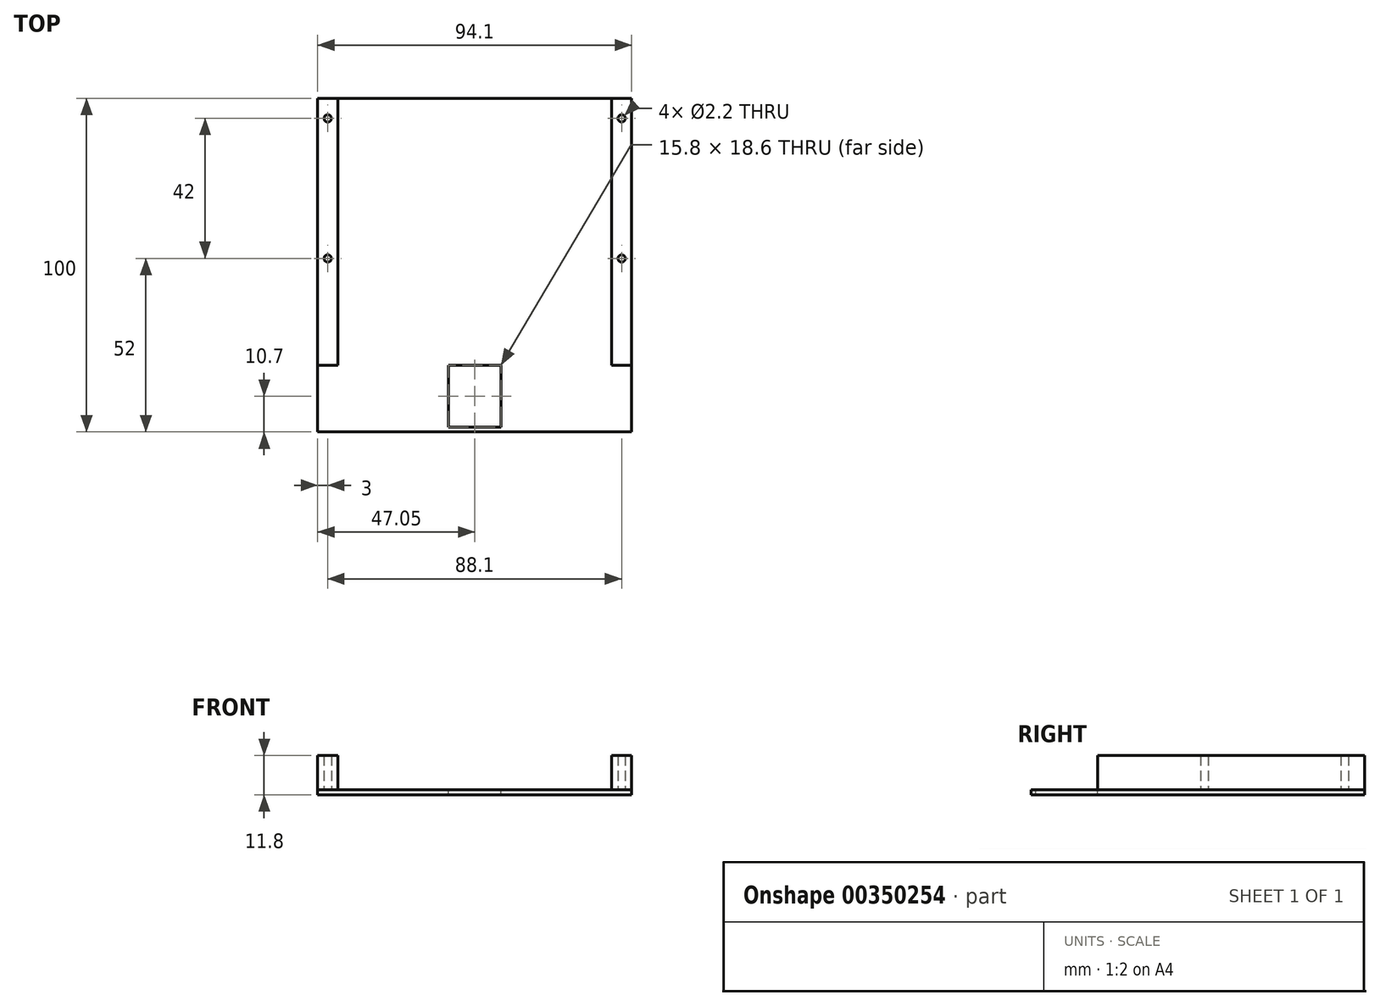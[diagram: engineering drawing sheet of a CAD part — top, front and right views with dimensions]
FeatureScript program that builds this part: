
annotation { "Feature Type Name" : "Feature", "Feature Type Description" : "" }
export const myFeature = defineFeature(function(context is Context, id is Id, definition is map)
    precondition{}
    {
        {
            var Q0;
            Q0=qCreatedBy(makeId("Top.planeOp"),FACE);
            var sketch = newSketch(context, id + "F0", { "sketchPlane" : qUnion([Q0])});
            skLineSegment(sketch, "E0.bottom", {"start": v(0, 0) * mm, "end": v(82.1, 0) * mm});
            skLineSegment(sketch, "E0.top", {"start": v(0, 80) * mm, "end": v(82.1, 80) * mm});
            skLineSegment(sketch, "E0.left", {"start": v(0, 0) * mm, "end": v(0, 80) * mm});
            skLineSegment(sketch, "E0.right", {"start": v(82.1, 0) * mm, "end": v(82.1, 80) * mm});
            skLineSegment(sketch, "E1.bottom", {"start": v(82.1, 80) * mm, "end": v(88.1, 80) * mm});
            skLineSegment(sketch, "E1.top", {"start": v(82.1, 0) * mm, "end": v(88.1, 0) * mm});
            skLineSegment(sketch, "E1.left", {"start": v(82.1, 80) * mm, "end": v(82.1, 0) * mm});
            skLineSegment(sketch, "E1.right", {"start": v(88.1, 80) * mm, "end": v(88.1, 0) * mm});
            skLineSegment(sketch, "E2.bottom", {"start": v(0, 0) * mm, "end": v(-6, 0) * mm});
            skLineSegment(sketch, "E2.top", {"start": v(0, 80) * mm, "end": v(-6, 80) * mm});
            skLineSegment(sketch, "E2.right", {"start": v(-6, 0) * mm, "end": v(-6, 80) * mm});
            skLineSegment(sketch, "E3.bottom", {"start": v(-6, 0) * mm, "end": v(88.1, 0) * mm});
            skLineSegment(sketch, "E3.top", {"start": v(-6, -20) * mm, "end": v(88.1, -20) * mm});
            skLineSegment(sketch, "E3.left", {"start": v(-6, 0) * mm, "end": v(-6, -20) * mm});
            skLineSegment(sketch, "E3.right", {"start": v(88.1, 0) * mm, "end": v(88.1, -20) * mm});
            skLineSegment(sketch, "E4.bottom", {"start": v(-6, 0) * mm, "end": v(33.15, 0) * mm});
            skLineSegment(sketch, "E4.top", {"start": v(-6, -20) * mm, "end": v(33.15, -20) * mm});
            skLineSegment(sketch, "E4.right", {"start": v(33.15, 0) * mm, "end": v(33.15, -20) * mm});
            skLineSegment(sketch, "E5.bottom", {"start": v(88.1, 0) * mm, "end": v(48.95, 0) * mm});
            skLineSegment(sketch, "E5.top", {"start": v(88.1, -20) * mm, "end": v(48.95, -20) * mm});
            skLineSegment(sketch, "E5.right", {"start": v(48.95, 0) * mm, "end": v(48.95, -20) * mm});
            skLineSegment(sketch, "E6.bottom", {"start": v(33.15, 0) * mm, "end": v(48.95, 0) * mm});
            skLineSegment(sketch, "E6.top", {"start": v(33.15, -20) * mm, "end": v(48.95, -20) * mm});
            skLineSegment(sketch, "E7.top", {"start": v(33.15, -18.6) * mm, "end": v(48.95, -18.6) * mm});
            skLineSegment(sketch, "E7.left", {"start": v(33.15, 0) * mm, "end": v(33.15, -18.6) * mm});
            skLineSegment(sketch, "E7.right", {"start": v(48.95, 0) * mm, "end": v(48.95, -18.6) * mm});
            skLineSegment(sketch, "E8.bottom", {"start": v(33.15, -18.6) * mm, "end": v(38.15, -18.6) * mm});
            skLineSegment(sketch, "E8.top", {"start": v(33.15, -20) * mm, "end": v(38.15, -20) * mm});
            skLineSegment(sketch, "E8.left", {"start": v(33.15, -18.6) * mm, "end": v(33.15, -20) * mm});
            skLineSegment(sketch, "E8.right", {"start": v(38.15, -18.6) * mm, "end": v(38.15, -20) * mm});
            skLineSegment(sketch, "E9.bottom", {"start": v(48.95, -18.6) * mm, "end": v(43.95, -18.6) * mm});
            skLineSegment(sketch, "E9.top", {"start": v(48.95, -20) * mm, "end": v(43.95, -20) * mm});
            skLineSegment(sketch, "E9.left", {"start": v(48.95, -18.6) * mm, "end": v(48.95, -20) * mm});
            skLineSegment(sketch, "E9.right", {"start": v(43.95, -18.6) * mm, "end": v(43.95, -20) * mm});
            skLineSegment(sketch, "E10.bottom", {"start": v(38.15, -18.6) * mm, "end": v(43.95, -18.6) * mm});
            skLineSegment(sketch, "E10.top", {"start": v(38.15, -20) * mm, "end": v(43.95, -20) * mm});
            skPoint(sketch, "E11", {"position": v(-3, 74) * mm});
            skPoint(sketch, "E11.positionSnap0", {"position": v(-3, 80) * mm});
            skPoint(sketch, "E12", {"position": v(85.1, 74) * mm});
            skPoint(sketch, "E12.positionSnap0", {"position": v(85.1, 80) * mm});
            skPoint(sketch, "E13", {"position": v(-3, -10) * mm});
            skPoint(sketch, "E13.positionSnap0", {"position": v(-6, -10) * mm});
            skPoint(sketch, "E14.positionSnap0", {"position": v(88.1, -10) * mm});
            skPoint(sketch, "E15", {"position": v(54.95, -10) * mm});
            skPoint(sketch, "E15.positionSnap0", {"position": v(48.95, -10) * mm});
            skPoint(sketch, "E16", {"position": v(27.15, -10) * mm});
            skPoint(sketch, "E16.positionSnap0", {"position": v(33.15, -10) * mm});
            skPoint(sketch, "E17", {"position": v(85.1, -10) * mm});
            skLineSegment(sketch, "E18", {"start": v(85.1, 74) * mm, "end": v(85.1, -10) * mm, "construction": true});
            skLineSegment(sketch, "E19", {"start": v(-3, 74) * mm, "end": v(-3, -10) * mm, "construction": true});
            skPoint(sketch, "E20", {"position": v(85.1, 32) * mm});
            skPoint(sketch, "E21", {"position": v(-3, 32) * mm});
            skSolve(sketch);
        }
        {
            var Q0;
            Q0=makeQuery(id+"F0.imprint","IMPRINT",FACE,{"disambiguationData":[TD([[makeQuery(id+"F0.imprint","IMPRINT",EDGE,{"derivedFrom":sQuery(id+"F0.wireOp",EDGE,"E2.top")}),1.0]])]});
            var Q1;
            Q1=makeQuery(id+"F0.imprint","IMPRINT",FACE,{"disambiguationData":[TD([[makeQuery(id+"F0.imprint","IMPRINT",EDGE,{"derivedFrom":sQuery(id+"F0.wireOp",EDGE,"E4.top")}),1.0]])]});
            var Q2;
            Q2=makeQuery(id+"F0.imprint","IMPRINT",FACE,{"disambiguationData":[TD([[makeQuery(id+"F0.imprint","IMPRINT",EDGE,{"derivedFrom":sQuery(id+"F0.wireOp",EDGE,"E6.top")}),1.0]])]});
            var Q3;
            Q3=makeQuery(id+"F0.imprint","IMPRINT",FACE,{"disambiguationData":[TD([[makeQuery(id+"F0.imprint","IMPRINT",EDGE,{"derivedFrom":sQuery(id+"F0.wireOp",EDGE,"E5.top")}),-1.0]])]});
            var Q4;
            Q4=makeQuery(id+"F0.imprint","IMPRINT",FACE,{"disambiguationData":[TD([[makeQuery(id+"F0.imprint","IMPRINT",EDGE,{"derivedFrom":sQuery(id+"F0.wireOp",EDGE,"E1.bottom")}),-1.0]])]});
            var Q5;
            Q5=makeQuery(id+"F0.imprint","IMPRINT",FACE,{"disambiguationData":[TD([[makeQuery(id+"F0.imprint","IMPRINT",EDGE,{"derivedFrom":sQuery(id+"F0.wireOp",EDGE,"E8.bottom")}),-1.0]])]});
            var Q6;
            Q6=makeQuery(id+"F0.imprint","IMPRINT",FACE,{"disambiguationData":[TD([[makeQuery(id+"F0.imprint","IMPRINT",EDGE,{"derivedFrom":sQuery(id+"F0.wireOp",EDGE,"E9.bottom")}),1.0]])]});
            extrude(context, id + "F1", {"entities" : qUnion([Q0, Q1, Q2, Q3, Q4, Q5, Q6]), "offsetDistance" : 25 * mm, "depth" : 10.3 * mm});
        }
        {
            var Q0;
            Q0 = qSketchRegion(id + "F0", true);
            var Q1;
            Q1=makeQuery(id+"F0.imprint","IMPRINT",FACE,{"disambiguationData":[TD([[makeQuery(id+"F0.imprint","IMPRINT",EDGE,{"derivedFrom":sQuery(id+"F0.wireOp",EDGE,"E6.bottom")}),-1.0]])]});
            extrude(context, id + "F2", {"entities" : qUnion([Q0, Q1]), "oppositeDirection" : true, "offsetDistance" : 25 * mm, "depth" : 1.5 * mm});
        }
        {
            var Q0;
            Q0=sQuery(id+"F0.wireOp",VERTEX,"E11");
            var Q1;
            Q1=sQuery(id+"F0.wireOp",VERTEX,"E12");
            var Q2;
            Q2=sQuery(id+"F0.wireOp",VERTEX,"E20");
            var Q3;
            Q3=sQuery(id+"F0.wireOp",VERTEX,"E21");
            var Q4;
            Q4=sQuery(id+"F0.wireOp",VERTEX,"E13");
            var Q5;
            Q5=sQuery(id+"F0.wireOp",VERTEX,"E16");
            var Q6;
            Q6=sQuery(id+"F0.wireOp",VERTEX,"E15");
            var Q7;
            Q7=sQuery(id+"F0.wireOp",VERTEX,"E17");
            var Q8;
            Q8=makeQuery(id+"F1.opExtrude","SWEPT_BODY",BODY,{"disambiguationData":[OSD([sQuery(id+"F0.wireOp",EDGE,"E2.top"),sQuery(id+"F0.wireOp",EDGE,"E0.left"),sQuery(id+"F0.wireOp",EDGE,"E2.right"),sQuery(id+"F0.wireOp",EDGE,"E4.bottom"),sQuery(id+"F0.wireOp",EDGE,"E4.top"),sQuery(id+"F0.wireOp",EDGE,"E3.left"),sQuery(id+"F0.wireOp",EDGE,"E7.left"),sQuery(id+"F0.wireOp",EDGE,"E8.bottom"),sQuery(id+"F0.wireOp",EDGE,"E8.top"),sQuery(id+"F0.wireOp",EDGE,"E8.right")])]});
            var Q9;
            Q9=makeQuery(id+"F1.opExtrude","SWEPT_BODY",BODY,{"disambiguationData":[OSD([sQuery(id+"F0.wireOp",EDGE,"E1.bottom"),sQuery(id+"F0.wireOp",EDGE,"E1.left"),sQuery(id+"F0.wireOp",EDGE,"E1.right"),sQuery(id+"F0.wireOp",EDGE,"E5.bottom"),sQuery(id+"F0.wireOp",EDGE,"E5.top"),sQuery(id+"F0.wireOp",EDGE,"E3.right"),sQuery(id+"F0.wireOp",EDGE,"E7.right"),sQuery(id+"F0.wireOp",EDGE,"E9.bottom"),sQuery(id+"F0.wireOp",EDGE,"E9.top"),sQuery(id+"F0.wireOp",EDGE,"E9.right")])]});
            hole(context, id + "F3", {"style" : HoleStyle.SIMPLE, "endStyle" : HoleEndStyle.THROUGH, "oppositeDirection" : true, "holeDiameter" : 2.2 * mm, "majorDiameter" : 5 * mm, "isTappedThrough" : true, "tappedDepth" : 100 * mm, "tapClearance" : 3, "locations" : qUnion([Q0, Q1, Q2, Q3, Q4, Q5, Q6, Q7]), "scope" : qUnion([Q8, Q9])});
        }
    });
